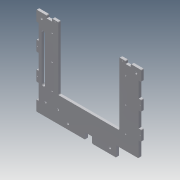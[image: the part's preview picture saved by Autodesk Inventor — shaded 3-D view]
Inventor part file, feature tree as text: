
AUTODESK INVENTOR PART (.ipt)
format: ipt  version: 2014 (Build 180170000, 170)  size: 311,808 bytes
history: native  units: mm
features: extrude x9, sketch x9, fillet x2
ambient origin geometry x8: Origin, YZ Plane, XZ Plane, XY Plane, X Axis, Y Axis, Z Axis, Center Point
bodies: Solid1 (feature_tree)
feature tree (20):
  extrude  "Extrusion1"  Depth=175.0mm
  extrude  "Extrusion2"  Depth=185.0mm
  extrude  "Extrusion3"  Depth=6.0mm TaperAngle=0.0deg
  extrude  "Extrusion4"  Depth=59.0mm
  extrude  "Extrusion5"  Depth=6.0mm TaperAngle=0.0deg
  extrude  "Extrusion6"  Depth=8.0mm
  extrude  "Extrusion7"  Depth=108.0mm
  extrude  "Extrusion8"  Depth=60.0mm
  extrude  "Extrusion9"  Depth=175.0mm
  fillet  "Fillet1"  Radius=3.2mm
  fillet  "Fillet2"  Radius=150.0mm
  sketch  "Sketch1"  dims[d0=175.0mm d1=87.5mm]
  sketch  "Sketch2"  dims[d2=145.0mm d4=185.0mm]
  sketch  "Sketch3"  dims[d5=250.0mm d6=6.0mm d7=0.0mm]
  sketch  "Sketch4"  dims[d8=3.0mm d9=0.0mm d10=59.0mm]
  sketch  "Sketch5"  dims[d11=25.0mm d13=6.0mm d14=0.0mm]
  sketch  "Sketch6"  dims[d15=35.0mm d16=8.0mm]
  sketch  "Sketch7"  dims[d17=108.0mm d18=40.0mm]
  sketch  "Sketch8"  dims[d19=10.0mm d20=0.0mm d21=60.0mm]
  sketch  "Sketch9"  dims[d22=60.0mm d23=175.0mm d24=3.2mm d25=150.0mm d26=15.0mm d27=10.0mm d28=0.0mm d29=50.0mm d30=54.0mm d31=3.0mm d32=4.4mm d33=30.0mm d34=15.0mm d35=10.0mm d36=0.0mm d37=2.0mm d38=16.0mm d39=15.0mm d40=10.0mm d41=0.0mm d42=12.5mm d43=50.0mm d44=50.0mm d45=5.4mm d46=12.5mm d47=12.5mm d48=12.5mm d49=5.4mm d50=25.0mm d51=6.1mm d52=25.0mm d53=25.0mm d54=2.2mm d55=12.5mm d56=12.5mm d57=10.0mm d58=0.0mm d59=2.0mm d60=12.5mm d63=10.0mm d64=0.0mm d66=25.0mm d68=8.0mm d69=8.0mm d70=25.0mm d71=12.5mm]
